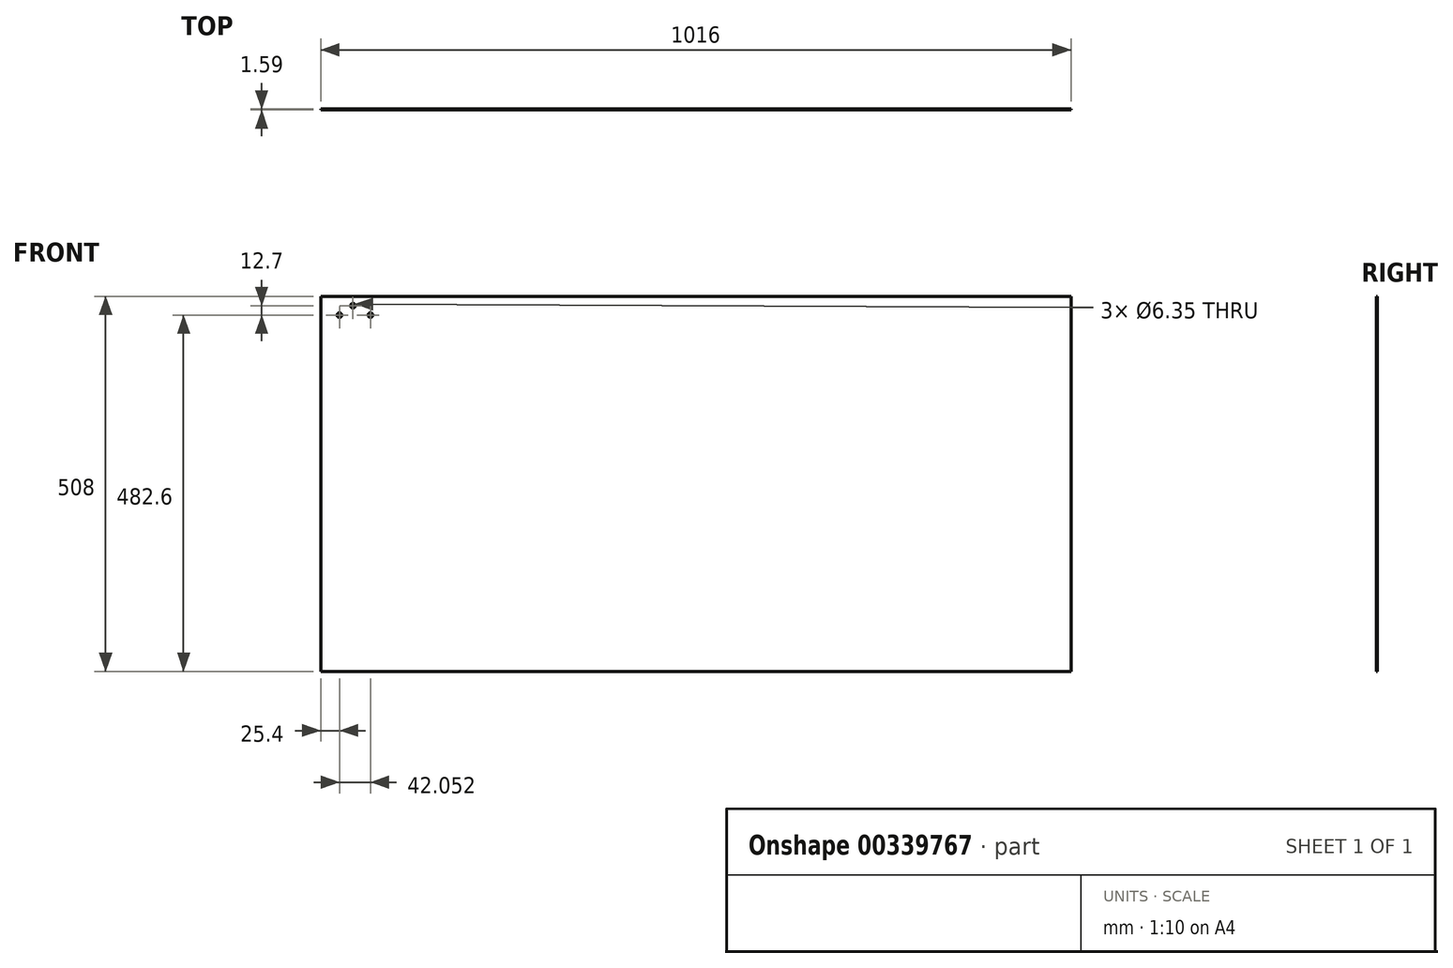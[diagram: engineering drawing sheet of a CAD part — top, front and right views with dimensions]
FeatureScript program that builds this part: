
annotation { "Feature Type Name" : "Feature", "Feature Type Description" : "" }
export const myFeature = defineFeature(function(context is Context, id is Id, definition is map)
    precondition{}
    {
        {
            var Q0;
            Q0=qCreatedBy(makeId("Front.planeOp"),FACE);
            var sketch = newSketch(context, id + "F0", { "sketchPlane" : qUnion([Q0])});
            skLineSegment(sketch, "E0.bottom", {"start": v(-508, 254) * mm, "end": v(508, 254) * mm});
            skLineSegment(sketch, "E0.top", {"start": v(-508, -254) * mm, "end": v(508, -254) * mm});
            skLineSegment(sketch, "E0.left", {"start": v(-508, 254) * mm, "end": v(-508, -254) * mm});
            skLineSegment(sketch, "E0.right", {"start": v(508, 254) * mm, "end": v(508, -254) * mm});
            skPoint(sketch, "E0.middle", {"position": v(0, 0) * mm});
            skCircle(sketch, "E1", {"center": v(-482.6, 228.6) * mm, "radius": 3.17 * mm});
            skCircle(sketch, "E2", {"center": v(-464.36, 241.3) * mm, "radius": 3.18 * mm});
            skCircle(sketch, "E3", {"center": v(-440.55, 228.6) * mm, "radius": 3.18 * mm});
            skSolve(sketch);
        }
        {
            var Q0;
            Q0 = qSketchRegion(id + "F0", true);
            extrude(context, id + "F1", {"entities" : qUnion([Q0]), "depth" : 1.59 * mm});
        }
    });
